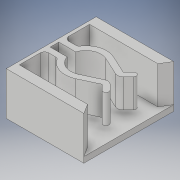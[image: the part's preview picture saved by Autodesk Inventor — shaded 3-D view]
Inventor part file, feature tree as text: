
AUTODESK INVENTOR PART (.ipt)
format: ipt  version: 2019.3 (Build 233278000, 278)  size: 192,000 bytes
history: native  units: mm
features: extrude x3, sketch x3, projected_geometry x1
ambient origin geometry x8: Origin, YZ Plane, XZ Plane, XY Plane, X Axis, Y Axis, Z Axis, Center Point
bodies: Solid1 (feature_tree)
feature tree (7):
  extrude  "Extrusion1"  Depth=10.0mm
  extrude  "Extrusion2"  Depth=2.0mm
  extrude  "Extrusion3"  Depth=2.0mm
  sketch  "Sketch1"  dims[d0=10.0mm d1=10.5mm]
  sketch  "Sketch2"  dims[d2=2.0mm d3=2.0mm]
  projected_geometry  "Projected Loop1"
  sketch  "Sketch3"  dims[d4=2.0mm d5=4.363323mm d6=1.5mm d7=19.198622mm d8=2.5mm d9=10.0mm d10=0.0mm d11=1.5mm d12=1.0mm d13=3.0mm d14=0.0mm d15=2.0mm d16=0.0mm]
